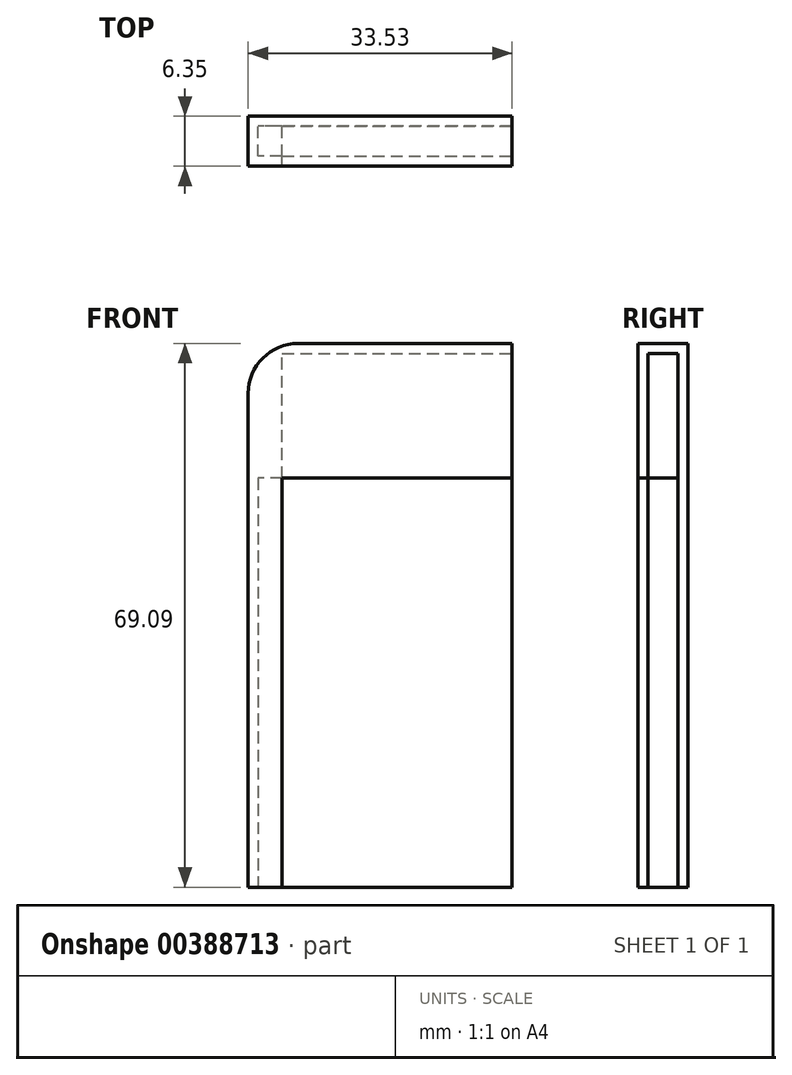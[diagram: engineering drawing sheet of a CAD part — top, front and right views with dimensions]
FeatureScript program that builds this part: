
annotation { "Feature Type Name" : "Feature", "Feature Type Description" : "" }
export const myFeature = defineFeature(function(context is Context, id is Id, definition is map)
    precondition{}
    {
        {
            var Q0;
            Q0=qCreatedBy(makeId("Front.planeOp"),FACE);
            var sketch = newSketch(context, id + "F0", { "sketchPlane" : qUnion([Q0])});
            skLineSegment(sketch, "E0.top", {"start": v(-27.18, 69.09) * mm, "end": v(0, 69.09) * mm});
            skLineSegment(sketch, "E0.left", {"start": v(-33.53, 0) * mm, "end": v(-33.53, 62.74) * mm});
            skPoint(sketch, "E1.top.end.orphan", {"position": v(-310.56, 69.09) * mm});
            skArc(sketch, "E2.filletArc", {"start": v(-27.18, 69.09) * mm, "mid": v(-31.67, 67.23) * mm, "end": v(-33.53, 62.74) * mm});
            skLineSegment(sketch, "E3.top", {"start": v(-29.22, 51.97) * mm, "end": v(0, 51.97) * mm});
            skLineSegment(sketch, "E3.left", {"start": v(-29.22, 0) * mm, "end": v(-29.22, 51.97) * mm});
            skLineSegment(sketch, "E4", {"start": v(-29.22, 0) * mm, "end": v(-33.53, 0) * mm});
            skLineSegment(sketch, "E5", {"start": v(0, 51.97) * mm, "end": v(0, 69.09) * mm});
            skSolve(sketch);
        }
        {
            var Q0;
            Q0 = qSketchRegion(id + "F0", true);
            extrude(context, id + "F1", {"entities" : qUnion([Q0]), "depth" : 6.35 * mm});
        }
        {
            var Q0;
            Q0=makeQuery(id+"F1.opExtrude","SWEPT_FACE",FACE,{"disambiguationData":[OSD([sQuery(id+"F0.wireOp",EDGE,"E4")])]});
            var sketch = newSketch(context, id + "F2", { "sketchPlane" : qUnion([Q0])});
            skLineSegment(sketch, "E6.bottom", {"start": v(-29.22, 5.08) * mm, "end": v(-32.26, 5.08) * mm});
            skLineSegment(sketch, "E6.top", {"start": v(-29.22, 1.27) * mm, "end": v(-32.26, 1.27) * mm});
            skLineSegment(sketch, "E6.left", {"start": v(-29.22, 5.08) * mm, "end": v(-29.22, 1.27) * mm});
            skLineSegment(sketch, "E6.right", {"start": v(-32.26, 5.08) * mm, "end": v(-32.26, 1.27) * mm});
            skSolve(sketch);
        }
        {
            var Q0;
            Q0=makeQuery(id+"F2.imprint","IMPRINT",FACE,{"disambiguationData":[TD([[makeQuery(id+"F2.imprint","IMPRINT",EDGE,{"derivedFrom":sQuery(id+"F2.wireOp",EDGE,"E6.bottom")}),1.0]])]});
            extrude(context, id + "F3", {"entities" : qUnion([Q0]), "operationType" : NewBodyOperationType.REMOVE, "oppositeDirection" : true, "depth" : 51.97 * mm});
        }
        {
            var Q0;
            Q0=makeQuery(id+"F1.opExtrude","SWEPT_FACE",FACE,{"disambiguationData":[OSD([sQuery(id+"F0.wireOp",EDGE,"E5")])]});
            var sketch = newSketch(context, id + "F4", { "sketchPlane" : qUnion([Q0])});
            skLineSegment(sketch, "E7.bottom", {"start": v(-5.08, 51.97) * mm, "end": v(-1.27, 51.97) * mm});
            skLineSegment(sketch, "E7.top", {"start": v(-5.08, 67.82) * mm, "end": v(-1.27, 67.82) * mm});
            skLineSegment(sketch, "E7.left", {"start": v(-5.08, 51.97) * mm, "end": v(-5.08, 67.82) * mm});
            skLineSegment(sketch, "E7.right", {"start": v(-1.27, 51.97) * mm, "end": v(-1.27, 67.82) * mm});
            skSolve(sketch);
        }
        {
            var Q0;
            Q0=makeQuery(id+"F4.imprint","IMPRINT",FACE,{"disambiguationData":[TD([[makeQuery(id+"F4.imprint","IMPRINT",EDGE,{"derivedFrom":sQuery(id+"F4.wireOp",EDGE,"E7.bottom")}),1.0]])]});
            extrude(context, id + "F5", {"entities" : qUnion([Q0]), "operationType" : NewBodyOperationType.REMOVE, "oppositeDirection" : true, "depth" : 29.2 * mm});
        }
        {
            var Q0;
            {var subQ0=sQuery(id+"F2.wireOp",EDGE,"E6.top");var subQ3=sQuery(id+"F0.wireOp",EDGE,"E3.left");Q0=makeQuery(id+"F3.boolean.opBoolean","SPLIT",FACE,{"disambiguationData":[TD([makeQuery(id+"F3.opExtrude","SWEPT_FACE",FACE,{"disambiguationData":[OSD([subQ0])]})])],"derivedFrom":makeQuery(id+"F1.opExtrude","SWEPT_FACE",FACE,{"disambiguationData":[OSD([subQ3])]})});}
            var sketch = newSketch(context, id + "F6", { "sketchPlane" : qUnion([Q0])});
            skLineSegment(sketch, "E8.bottom", {"start": v(-1.27, 0) * mm, "end": v(0, 0) * mm});
            skLineSegment(sketch, "E8.top", {"start": v(-1.27, 51.97) * mm, "end": v(0, 51.97) * mm});
            skLineSegment(sketch, "E8.left", {"start": v(-1.27, 0) * mm, "end": v(-1.27, 51.97) * mm});
            skLineSegment(sketch, "E8.right", {"start": v(0, 0) * mm, "end": v(0, 51.97) * mm});
            skSolve(sketch);
        }
        {
            var Q0;
            Q0 = qSketchRegion(id + "F6", true);
            var Q1;
            Q1=makeQuery(id+"F1.opExtrude","SWEPT_FACE",FACE,{"disambiguationData":[OSD([sQuery(id+"F0.wireOp",EDGE,"E5")])]});
            extrude(context, id + "F7", {"entities" : qUnion([Q0]), "operationType" : NewBodyOperationType.ADD, "endBound" : BoundingType.UP_TO_SURFACE, "endBoundEntityFace" : qUnion([Q1]), "depth" : 25.4 * mm});
        }
    });
